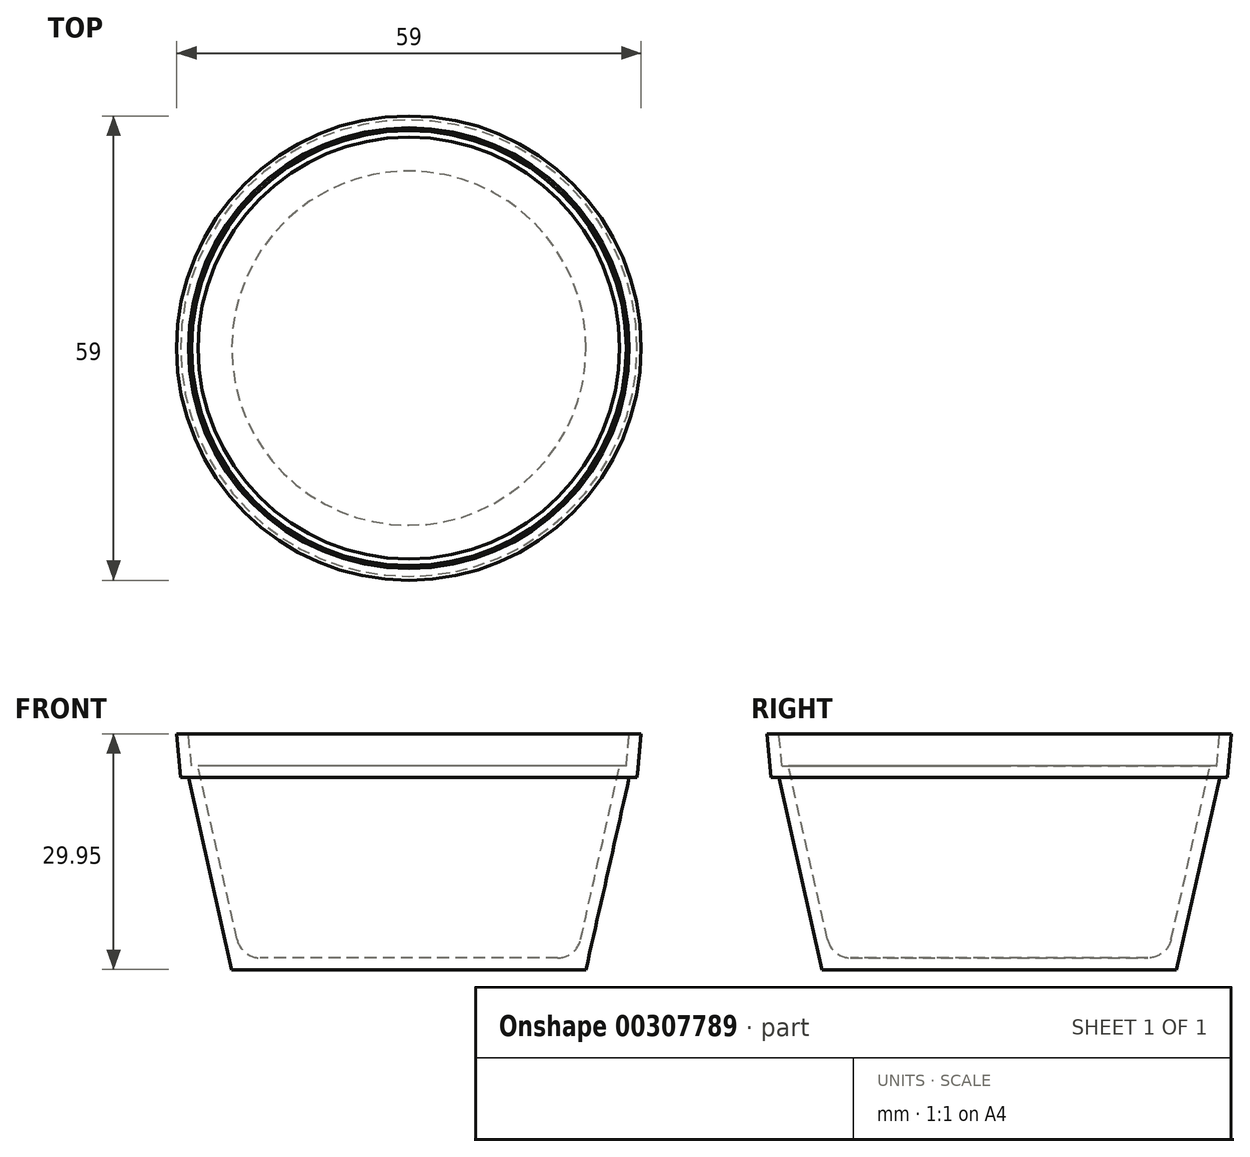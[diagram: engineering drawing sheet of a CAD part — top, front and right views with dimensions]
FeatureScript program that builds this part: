
annotation { "Feature Type Name" : "Feature", "Feature Type Description" : "" }
export const myFeature = defineFeature(function(context is Context, id is Id, definition is map)
    precondition{}
    {
        {
            var Q0;
            Q0=qCreatedBy(makeId("Front.planeOp"),FACE);
            var sketch = newSketch(context, id + "F0", { "sketchPlane" : qUnion([Q0])});
            skLineSegment(sketch, "E0", {"start": v(-22.98, 3.68) * mm, "end": v(-0.48, 3.68) * mm});
            skLineSegment(sketch, "E1", {"start": v(-22.98, 33.68) * mm, "end": v(-22.98, 3.68) * mm});
            skLineSegment(sketch, "E2", {"start": v(-0.48, 3.68) * mm, "end": v(5, 28.07) * mm});
            skLineSegment(sketch, "E3", {"start": v(5, 28.07) * mm, "end": v(6, 28.07) * mm});
            skLineSegment(sketch, "E4", {"start": v(6.52, 33.63) * mm, "end": v(-22.98, 33.68) * mm});
            skLineSegment(sketch, "E5", {"start": v(6.52, 33.63) * mm, "end": v(6, 28.07) * mm});
            skSolve(sketch);
        }
        {
            var Q0;
            Q0=makeQuery(id+"F0.imprint","IMPRINT",FACE,{"disambiguationData":[TD([[makeQuery(id+"F0.imprint","IMPRINT",EDGE,{"derivedFrom":sQuery(id+"F0.wireOp",EDGE,"E0")}),1.0]])]});
            var Q1;
            Q1=sQuery(id+"F0.wireOp",EDGE,"E1");
            revolve(context, id + "F1", {"entities" : qUnion([Q0]), "axis" : qUnion([Q1]), "revolveType" : RevolveType.FULL});
        }
        {
            var Q0;
            Q0=makeQuery(id+"F1.opRevolve","SWEPT_FACE",FACE,{"disambiguationData":[OSD([sQuery(id+"F0.wireOp",EDGE,"E4")])]});
            shell(context, id + "F2", {"entities" : qUnion([Q0]), "thickness" : 1.5 * mm});
        }
        {
            var Q0;
            Q0=makeQuery(id+"F2.opShell","OFFSET_EDGE",EDGE,{"disambiguationData":[OSD([sQuery(id+"F0.wireOp",EDGE,"E0"),sQuery(id+"F0.wireOp",EDGE,"E2")])]});
            fillet(context, id + "F3", {"entities" : qUnion([Q0]), "radius" : 3 * mm, "tangentPropagation" : true, "allowEdgeOverflow" : false});
        }
    });
